# Revit family: 22V-CH
name_source: partatom
category: Aparatos sanitarios
units: mm (PartAtom-declared; Revit-internal decimal feet)

## family parameters
Activar corte en vistas = No
Compartido = No
Corte con vacíos al cargar = No
Cota de conector redondo = Usar diámetro
Mantener orientación de anotación = No
Número OmniClass = 23.45.00.00
Punto de cálculo de habitación = No
Se basa en plano de trabajo = No
Siempre vertical = Sí
Tipo de pieza = Normal
Título OmniClass = Sanitary, Laundry, and Cleaning Equipment

## types (1)
- 22V-CH
    Comentarios de tipo = Drains
    Conexión AF = No
    Conexión de ventilación = Sí
    Connection = 2" Pipe
    Descripción = Coladera vertical corta de una boca con rejilla cuadrada de acero inoxidable. Incluye plato de drenado para evitar filtraciones.Contra con altura ajustable. Céspol que genera sello hidráulico para evitar malos olores. Fácil mantenimiento. Recomendable para baños, regaderas, vestíbulos y otras áreas interiores de pisos a nivel de planta y entrepisos.
    Elevación por defecto = 0"
    Fabricante = Helvex
    Material = Rejilla de acero inoxidable. Contra de latón. Cuerpo de hierro fundido con recubrimiento de 
pintura anticorrosiva.
    Modelo = 22V-CH
    Total Diameter = 7"
    Total Height = 5"

## geometry (parser evidence)
native form markers: Sweep x3
no freeform markers — native parametric forms only
